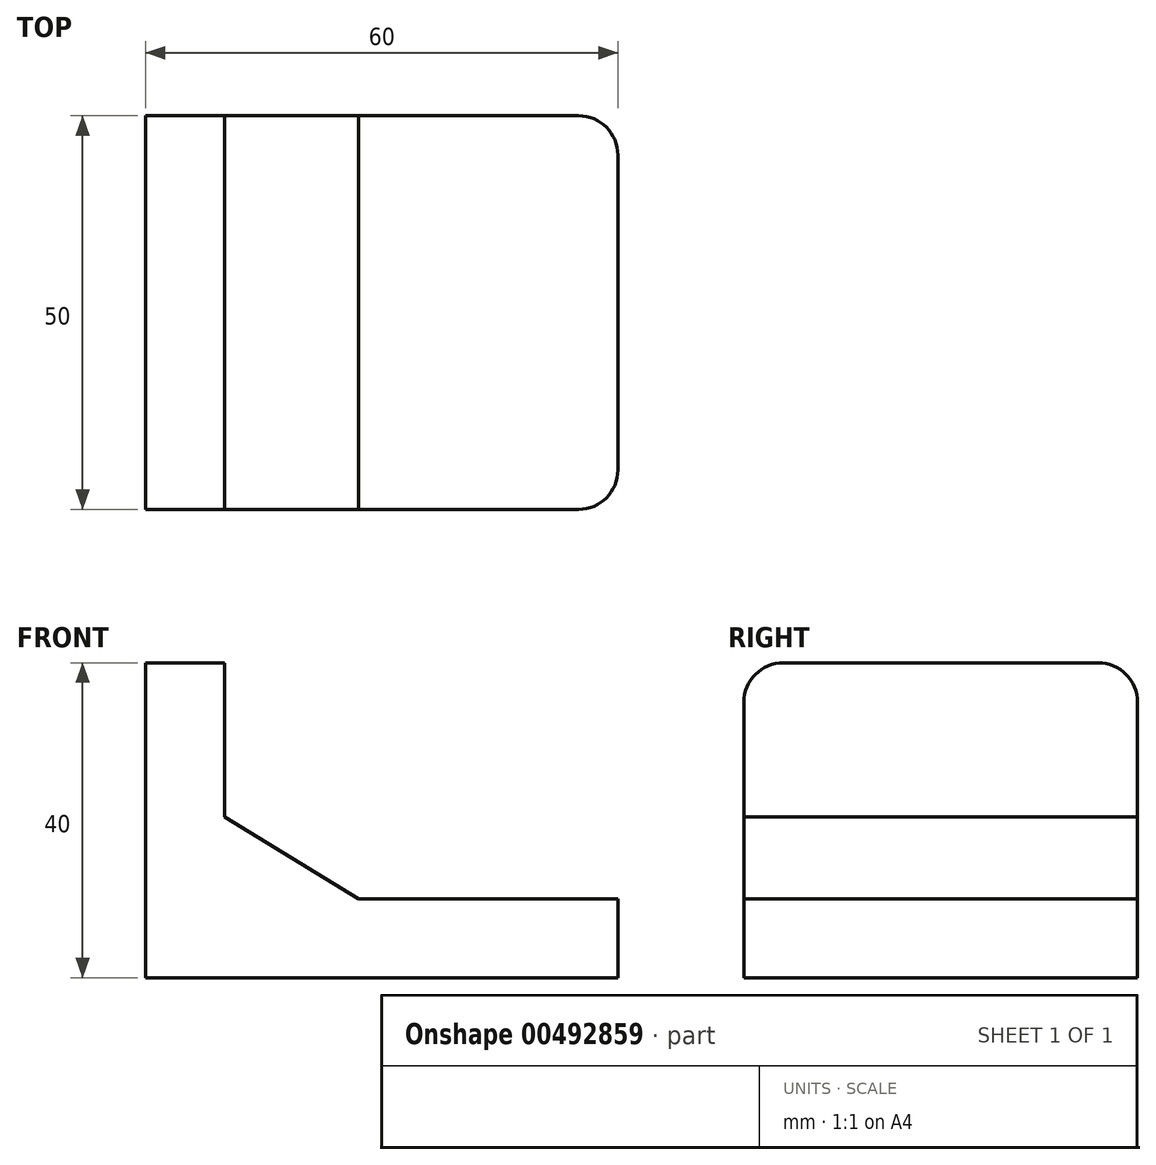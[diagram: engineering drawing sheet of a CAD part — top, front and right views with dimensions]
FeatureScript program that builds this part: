
annotation { "Feature Type Name" : "Feature", "Feature Type Description" : "" }
export const myFeature = defineFeature(function(context is Context, id is Id, definition is map)
    precondition{}
    {
        {
            var Q0;
            Q0=qCreatedBy(makeId("Front.planeOp"),FACE);
            var sketch = newSketch(context, id + "F0", { "sketchPlane" : qUnion([Q0])});
            skLineSegment(sketch, "E0", {"start": v(0, 0) * mm, "end": v(0, 40) * mm});
            skLineSegment(sketch, "E1", {"start": v(0, 40) * mm, "end": v(10, 40) * mm});
            skLineSegment(sketch, "E2", {"start": v(10, 40) * mm, "end": v(10, 20.43) * mm});
            skLineSegment(sketch, "E3", {"start": v(10, 20.43) * mm, "end": v(27.06, 10) * mm});
            skLineSegment(sketch, "E4", {"start": v(27.06, 10) * mm, "end": v(60, 10) * mm});
            skLineSegment(sketch, "E5", {"start": v(60, 10) * mm, "end": v(60, 0) * mm});
            skLineSegment(sketch, "E6", {"start": v(60, 0) * mm, "end": v(0, 0) * mm});
            skSolve(sketch);
        }
        {
            var Q0;
            Q0=makeQuery(id+"F0.imprint","IMPRINT",FACE,{"disambiguationData":[TD([[makeQuery(id+"F0.imprint","IMPRINT",EDGE,{"derivedFrom":sQuery(id+"F0.wireOp",EDGE,"E0")}),-1.0]])]});
            extrude(context, id + "F1", {"entities" : qUnion([Q0]), "oppositeDirection" : true, "depth" : 50 * mm});
        }
        {
            var Q0;
            Q0=makeQuery(id+"F1.opExtrude","CAP_EDGE",EDGE,{"disambiguationData":[OSD([sQuery(id+"F0.wireOp",EDGE,"E1")])],"isStart":true});
            var Q1;
            Q1=makeQuery(id+"F1.opExtrude","CAP_EDGE",EDGE,{"disambiguationData":[OSD([sQuery(id+"F0.wireOp",EDGE,"E1")])],"isStart":false});
            var Q2;
            Q2=makeQuery(id+"F1.opExtrude","CAP_EDGE",EDGE,{"disambiguationData":[OSD([sQuery(id+"F0.wireOp",EDGE,"E5")])],"isStart":true});
            var Q3;
            Q3=makeQuery(id+"F1.opExtrude","CAP_EDGE",EDGE,{"disambiguationData":[OSD([sQuery(id+"F0.wireOp",EDGE,"E5")])],"isStart":false});
            fillet(context, id + "F2", {"entities" : qUnion([Q0, Q1, Q2, Q3]), "radius" : 5 * mm, "tangentPropagation" : true, "allowEdgeOverflow" : false});
        }
    });
